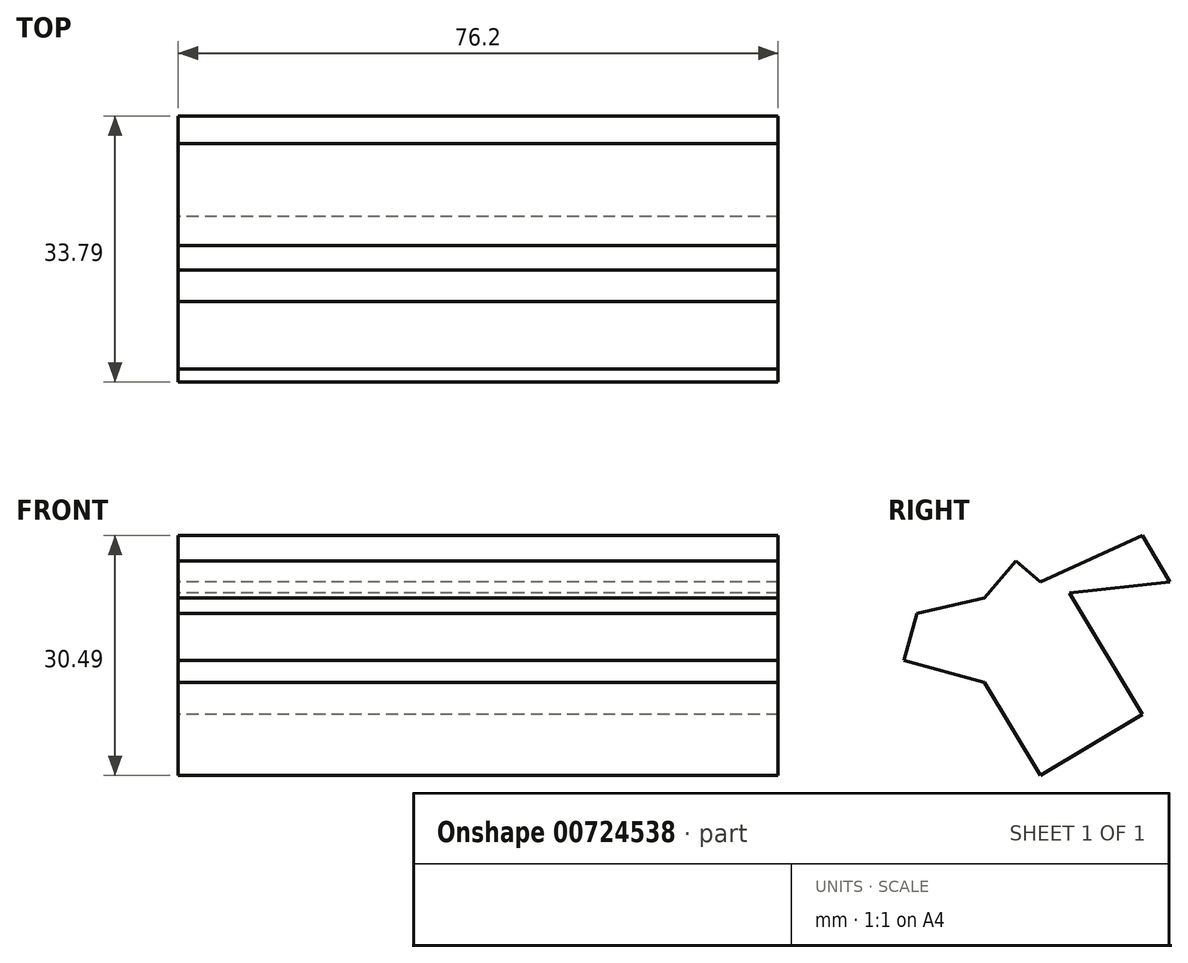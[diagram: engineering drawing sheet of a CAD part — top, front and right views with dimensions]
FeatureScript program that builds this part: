
annotation { "Feature Type Name" : "Feature", "Feature Type Description" : "" }
export const myFeature = defineFeature(function(context is Context, id is Id, definition is map)
    precondition{}
    {
        {
            var Q0;
            Q0=qCreatedBy(makeId("Right.planeOp"),FACE);
            var sketch = newSketch(context, id + "F0", { "sketchPlane" : qUnion([Q0])});
            skLineSegment(sketch, "E0", {"start": v(0, 36.86) * mm, "end": v(9.24, 21.42) * mm});
            skLineSegment(sketch, "E1", {"start": v(9.24, 21.42) * mm, "end": v(-3.7, 13.68) * mm});
            skLineSegment(sketch, "E2", {"start": v(-3.7, 13.68) * mm, "end": v(-10.8, 25.53) * mm});
            skLineSegment(sketch, "E3", {"start": v(-10.8, 25.53) * mm, "end": v(-21.02, 28.33) * mm});
            skLineSegment(sketch, "E4", {"start": v(-21.02, 28.33) * mm, "end": v(-19.39, 34.3) * mm});
            skLineSegment(sketch, "E5", {"start": v(-19.39, 34.3) * mm, "end": v(-10.8, 36.25) * mm});
            skLineSegment(sketch, "E6", {"start": v(-10.8, 36.25) * mm, "end": v(-6.8, 40.92) * mm});
            skLineSegment(sketch, "E7", {"start": v(-6.8, 40.92) * mm, "end": v(-3.7, 38.27) * mm});
            skLineSegment(sketch, "E8", {"start": v(-3.7, 38.27) * mm, "end": v(9.24, 44.17) * mm});
            skLineSegment(sketch, "E9", {"start": v(9.24, 44.17) * mm, "end": v(12.77, 38.27) * mm});
            skLineSegment(sketch, "E10", {"start": v(12.77, 38.27) * mm, "end": v(0, 36.86) * mm});
            skSolve(sketch);
        }
        {
            var Q0;
            Q0=makeQuery(id+"F0.imprint","IMPRINT",FACE,{"disambiguationData":[TD([[makeQuery(id+"F0.imprint","IMPRINT",EDGE,{"derivedFrom":sQuery(id+"F0.wireOp",EDGE,"E0")}),-1.0]])]});
            extrude(context, id + "F1", {"entities" : qUnion([Q0]), "depth" : 25.4 * mm, "offsetDistance" : 25.4 * mm});
        }
        {
            var Q0;
            Q0=makeQuery(id+"F1.opExtrude","CAP_FACE",FACE,{"disambiguationData":[OSD([sQuery(id+"F0.wireOp",EDGE,"E0"),sQuery(id+"F0.wireOp",EDGE,"E1"),sQuery(id+"F0.wireOp",EDGE,"E2"),sQuery(id+"F0.wireOp",EDGE,"E3"),sQuery(id+"F0.wireOp",EDGE,"E4"),sQuery(id+"F0.wireOp",EDGE,"E5"),sQuery(id+"F0.wireOp",EDGE,"E6"),sQuery(id+"F0.wireOp",EDGE,"E7"),sQuery(id+"F0.wireOp",EDGE,"E8"),sQuery(id+"F0.wireOp",EDGE,"E9"),sQuery(id+"F0.wireOp",EDGE,"E10")])],"isStart":true});
            extrude(context, id + "F2", {"entities" : qUnion([Q0]), "operationType" : NewBodyOperationType.ADD, "depth" : 25.4 * mm, "offsetDistance" : 25.4 * mm});
        }
        {
            var Q0;
            Q0=makeQuery(id+"F2.opExtrude","CAP_FACE",FACE,{"disambiguationData":[OSD([sQuery(id+"F0.wireOp",EDGE,"E0"),sQuery(id+"F0.wireOp",EDGE,"E1"),sQuery(id+"F0.wireOp",EDGE,"E2"),sQuery(id+"F0.wireOp",EDGE,"E3"),sQuery(id+"F0.wireOp",EDGE,"E4"),sQuery(id+"F0.wireOp",EDGE,"E5"),sQuery(id+"F0.wireOp",EDGE,"E6"),sQuery(id+"F0.wireOp",EDGE,"E7"),sQuery(id+"F0.wireOp",EDGE,"E8"),sQuery(id+"F0.wireOp",EDGE,"E9"),sQuery(id+"F0.wireOp",EDGE,"E10")])],"isStart":false});
            extrude(context, id + "F3", {"entities" : qUnion([Q0]), "operationType" : NewBodyOperationType.ADD, "depth" : 25.4 * mm, "offsetDistance" : 25.4 * mm});
        }
    });
